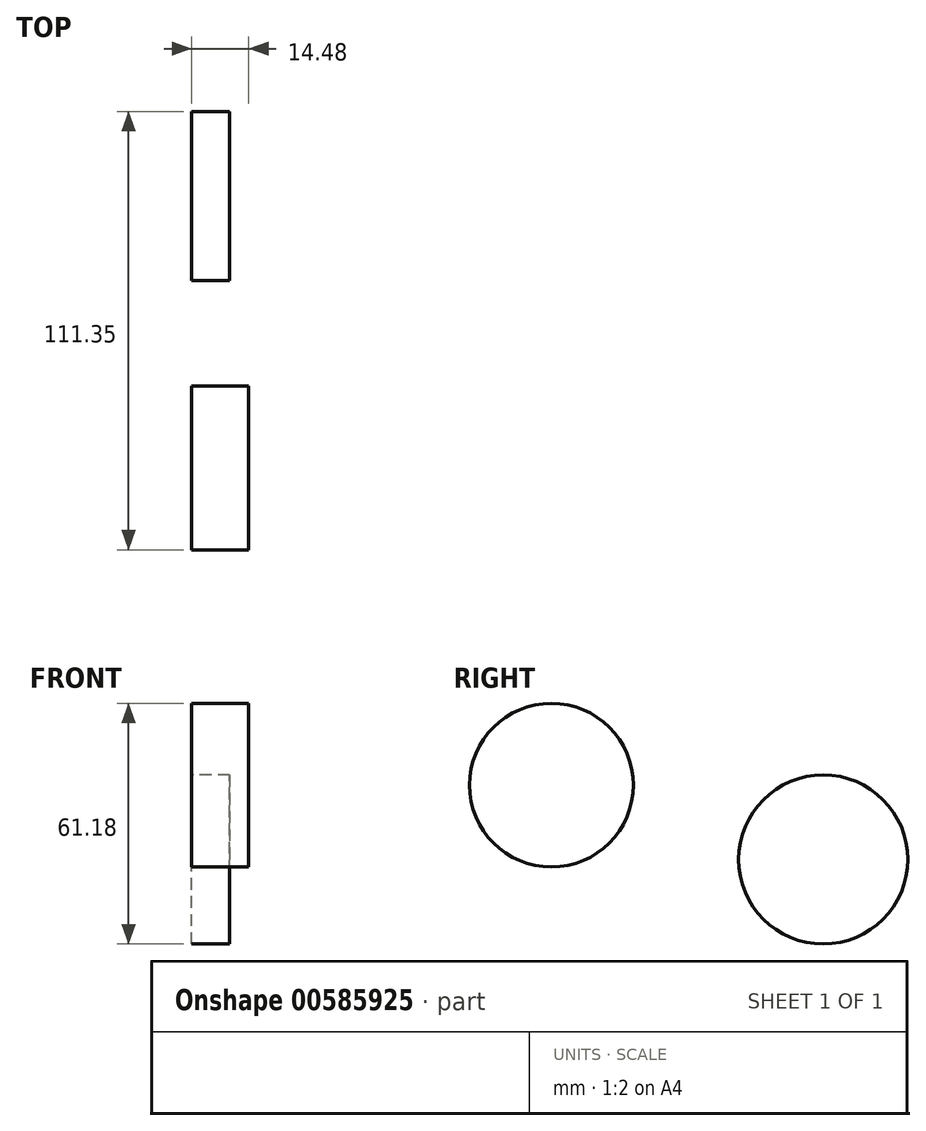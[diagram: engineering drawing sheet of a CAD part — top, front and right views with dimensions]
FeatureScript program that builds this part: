
annotation { "Feature Type Name" : "Feature", "Feature Type Description" : "" }
export const myFeature = defineFeature(function(context is Context, id is Id, definition is map)
    precondition{}
    {
        {
            var Q0;
            Q0=qCreatedBy(makeId("Right.planeOp"),FACE);
            var sketch = newSketch(context, id + "F0", { "sketchPlane" : qUnion([Q0])});
            skCircle(sketch, "E0", {"center": v(-46.34, 14.08) * mm, "radius": 20.8 * mm});
            skSolve(sketch);
        }
        {
            var Q0;
            Q0=qCreatedBy(makeId("Right.planeOp"),FACE);
            var sketch = newSketch(context, id + "F1", { "sketchPlane" : qUnion([Q0])});
            skCircle(sketch, "E1", {"center": v(22.73, -4.8) * mm, "radius": 21.48 * mm});
            skSolve(sketch);
        }
        {
            var Q0;
            Q0=makeQuery(id+"F0.imprint","IMPRINT",FACE,{"disambiguationData":[TD([[makeQuery(id+"F0.imprint","IMPRINT",EDGE,{"derivedFrom":sQuery(id+"F0.wireOp",EDGE,"E0")}),1.0]])]});
            extrude(context, id + "F2", {"entities" : qUnion([Q0]), "depth" : 14.48 * mm, "offsetDistance" : 25.4 * mm});
        }
        {
            var Q0;
            Q0=makeQuery(id+"F1.imprint","IMPRINT",FACE,{"disambiguationData":[TD([[makeQuery(id+"F1.imprint","IMPRINT",EDGE,{"derivedFrom":sQuery(id+"F1.wireOp",EDGE,"E1")}),1.0]])]});
            extrude(context, id + "F3", {"entities" : qUnion([Q0]), "depth" : 9.65 * mm, "offsetDistance" : 25.4 * mm});
        }
    });
